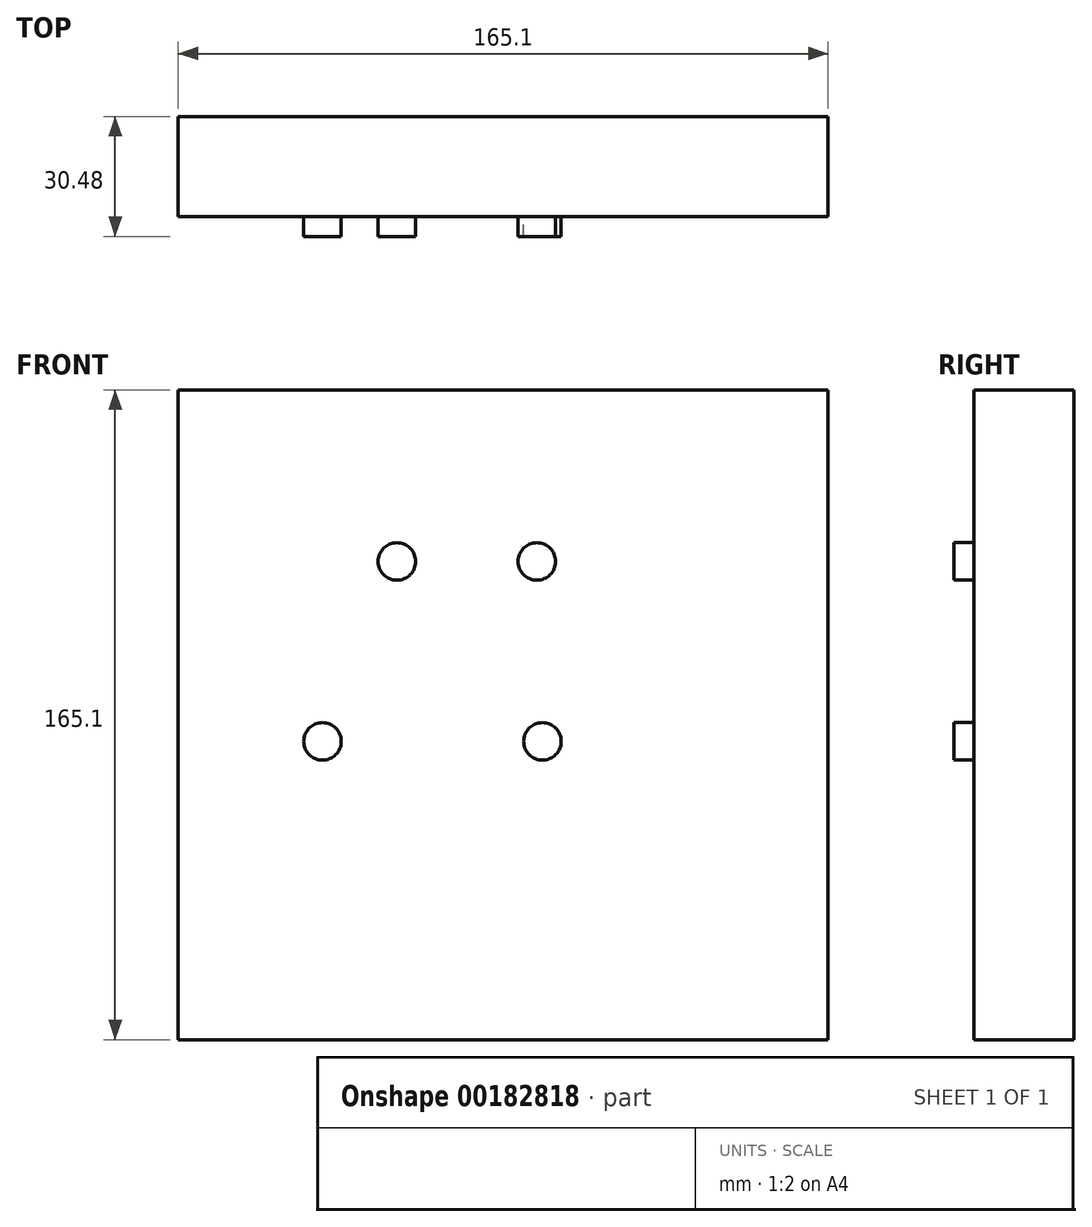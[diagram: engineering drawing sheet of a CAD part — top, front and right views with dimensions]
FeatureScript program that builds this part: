
annotation { "Feature Type Name" : "Feature", "Feature Type Description" : "" }
export const myFeature = defineFeature(function(context is Context, id is Id, definition is map)
    precondition{}
    {
        {
            var Q0;
            Q0=qCreatedBy(makeId("Front.planeOp"),FACE);
            var sketch = newSketch(context, id + "F0", { "sketchPlane" : qUnion([Q0])});
            skLineSegment(sketch, "E0.bottom", {"start": v(82.55, -82.55) * mm, "end": v(-82.55, -82.55) * mm});
            skLineSegment(sketch, "E0.top", {"start": v(82.55, 82.55) * mm, "end": v(-82.55, 82.55) * mm});
            skLineSegment(sketch, "E0.left", {"start": v(82.55, -82.55) * mm, "end": v(82.55, 82.55) * mm});
            skLineSegment(sketch, "E0.right", {"start": v(-82.55, -82.55) * mm, "end": v(-82.55, 82.55) * mm});
            skPoint(sketch, "E0.middle", {"position": v(0, 0) * mm});
            skSolve(sketch);
        }
        {
            var Q0;
            Q0 = qSketchRegion(id + "F0", true);
            extrude(context, id + "F1", {"entities" : qUnion([Q0]), "depth" : 25.4 * mm});
        }
        {
            var Q0;
            Q0=makeQuery(id+"F1.opExtrude","CAP_FACE",FACE,{"disambiguationData":[OSD([sQuery(id+"F0.wireOp",EDGE,"E0.bottom"),sQuery(id+"F0.wireOp",EDGE,"E0.top"),sQuery(id+"F0.wireOp",EDGE,"E0.left"),sQuery(id+"F0.wireOp",EDGE,"E0.right")])],"isStart":false});
            var sketch = newSketch(context, id + "F2", { "sketchPlane" : qUnion([Q0])});
            skCircle(sketch, "E1", {"center": v(-27, 38.94) * mm, "radius": 4.76 * mm});
            skCircle(sketch, "E2", {"center": v(8.56, 38.94) * mm, "radius": 4.76 * mm});
            skCircle(sketch, "E3", {"center": v(9.99, -6.78) * mm, "radius": 4.76 * mm});
            skCircle(sketch, "E4", {"center": v(-45.9, -6.78) * mm, "radius": 4.76 * mm});
            skSolve(sketch);
        }
        {
            var Q0;
            Q0=makeQuery(id+"F2.imprint","IMPRINT",FACE,{"disambiguationData":[TD([[makeQuery(id+"F2.imprint","IMPRINT",EDGE,{"derivedFrom":sQuery(id+"F2.wireOp",EDGE,"E1")}),1.0]])]});
            var Q1;
            Q1=makeQuery(id+"F2.imprint","IMPRINT",FACE,{"disambiguationData":[TD([[makeQuery(id+"F2.imprint","IMPRINT",EDGE,{"derivedFrom":sQuery(id+"F2.wireOp",EDGE,"E2")}),1.0]])]});
            var Q2;
            Q2=makeQuery(id+"F2.imprint","IMPRINT",FACE,{"disambiguationData":[TD([[makeQuery(id+"F2.imprint","IMPRINT",EDGE,{"derivedFrom":sQuery(id+"F2.wireOp",EDGE,"E4")}),1.0]])]});
            var Q3;
            Q3=makeQuery(id+"F2.imprint","IMPRINT",FACE,{"disambiguationData":[TD([[makeQuery(id+"F2.imprint","IMPRINT",EDGE,{"derivedFrom":sQuery(id+"F2.wireOp",EDGE,"E3")}),1.0]])]});
            extrude(context, id + "F3", {"entities" : qUnion([Q0, Q1, Q2, Q3]), "operationType" : NewBodyOperationType.ADD, "depth" : 5.08 * mm});
        }
    });
